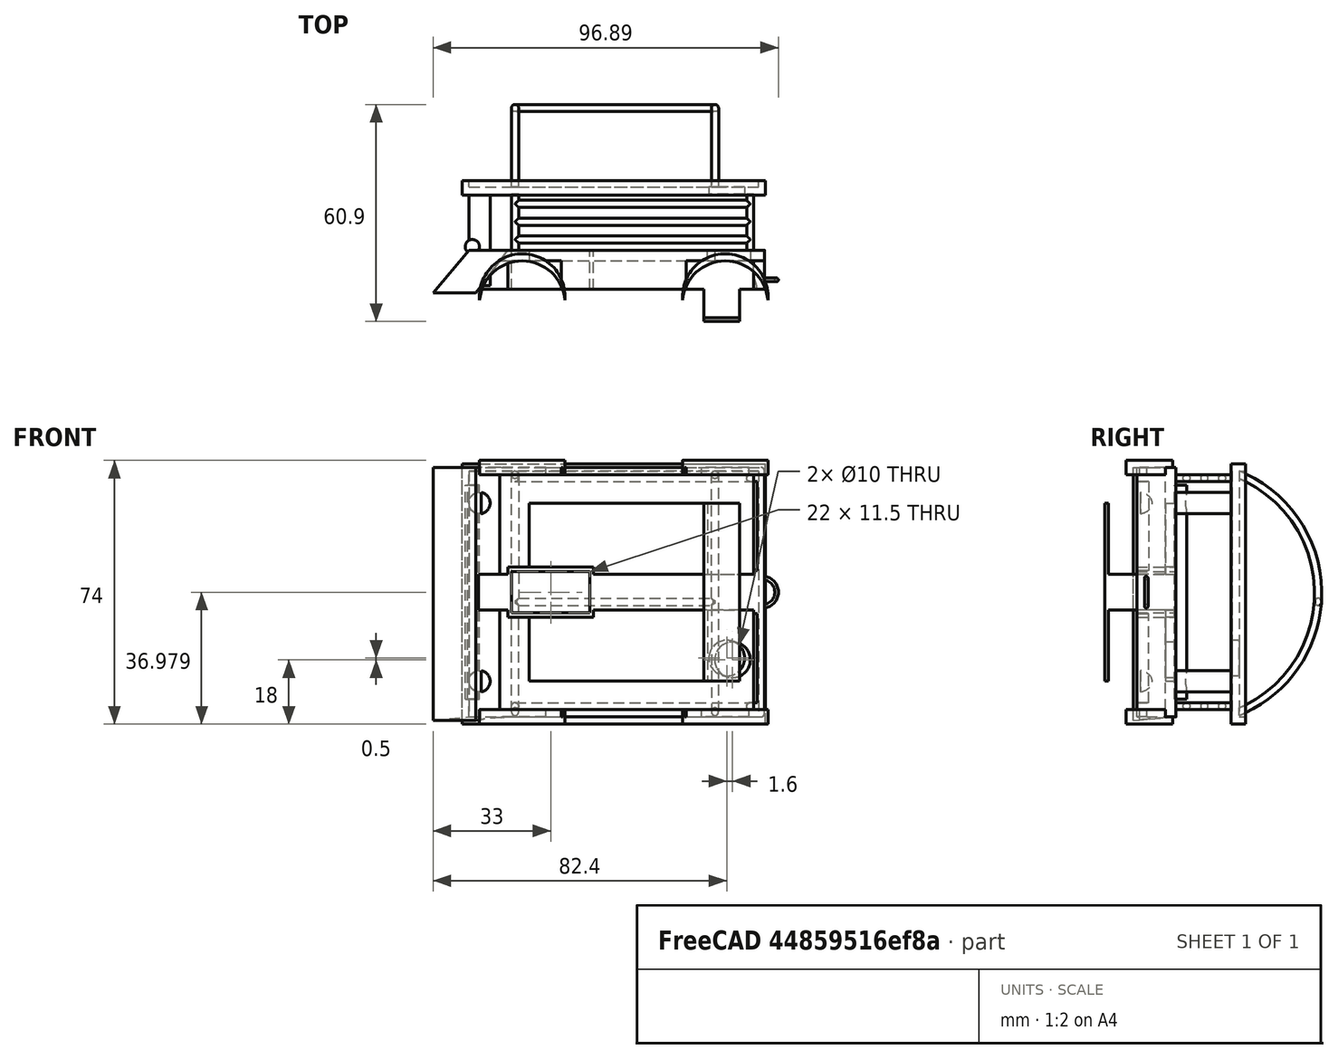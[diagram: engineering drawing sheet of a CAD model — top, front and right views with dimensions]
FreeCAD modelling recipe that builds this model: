
FCSTD DOCUMENT  (FreeCAD 0.18R4 (GitTag))
Label: Chasis Reto (Terminado)
License: All rights reserved
LicenseURL: http://en.wikipedia.org/wiki/All_rights_reserved
objects: Part::Cylinder×31, Part::Box×21, Part::MultiFuse×18, Part::Cut×15, Part::Torus×3, Part::Fillet×1, Part::Wedge×1
note: 90 computed .brp shape members not serialized (recipe doc carries the construction recipe); baked Part::Feature solids carry a one-line shape summary decoded from their .brp

FEATURE [Part::Cylinder] Cylinder  label="Cilindro"
  Angle = 360
  AttacherType = Attacher::AttachEngine3D
  Height = 4
  Radius = 12
FEATURE [Part::Cylinder] Cylinder001  label="Cilindro001"
  Angle = 360
  AttacherType = Attacher::AttachEngine3D
  Height = 4
  Placement = pos=(0,-2,0) rot=(0,0,1;0rad)
  Radius = 12
FEATURE [Part::Cut] Cut
  Base = -> Cylinder
  Placement = pos=(2,0,0) rot=(0,0,1;0rad)
  Refine = true
  Tool = -> Cylinder001
FEATURE [Part::Box] Box  label="Cubo"
  AttacherType = Attacher::AttachEngine3D
  Height = 70
  Length = 80
  Placement = pos=(-10,10,2) rot=(0,0,1;0rad)
  Width = 3
FEATURE [Part::Cylinder] Cylinder002  label="Cilindro002"
  Angle = 360
  AttacherType = Attacher::AttachEngine3D
  Height = 4
  Radius = 12
FEATURE [Part::Cylinder] Cylinder003  label="Cilindro003"
  Angle = 360
  AttacherType = Attacher::AttachEngine3D
  Height = 4
  Placement = pos=(0,-2,0) rot=(0,0,1;0rad)
  Radius = 12
FEATURE [Part::Cut] Cut001
  Base = -> Cylinder002
  Placement = pos=(2,0,70) rot=(0,0,1;0rad)
  Refine = true
  Tool = -> Cylinder003
FEATURE [Part::Cylinder] Cylinder004  label="Cilindro004"
  Angle = 360
  AttacherType = Attacher::AttachEngine3D
  Height = 4
  Radius = 12
FEATURE [Part::Cylinder] Cylinder005  label="Cilindro005"
  Angle = 360
  AttacherType = Attacher::AttachEngine3D
  Height = 4
  Placement = pos=(0,-2,0) rot=(0,0,1;0rad)
  Radius = 12
FEATURE [Part::Cut] Cut002
  Base = -> Cylinder004
  Placement = pos=(59,0,0) rot=(0,0,1;0rad)
  Refine = true
  Tool = -> Cylinder005
FEATURE [Part::Cylinder] Cylinder006  label="Cilindro006"
  Angle = 360
  AttacherType = Attacher::AttachEngine3D
  Height = 4
  Radius = 12
FEATURE [Part::Cylinder] Cylinder007  label="Cilindro007"
  Angle = 360
  AttacherType = Attacher::AttachEngine3D
  Height = 4
  Placement = pos=(0,-2,0) rot=(0,0,1;0rad)
  Radius = 12
FEATURE [Part::Cut] Cut003
  Base = -> Cylinder006
  Placement = pos=(59,0,70) rot=(0,0,1;0rad)
  Refine = true
  Tool = -> Cylinder007
FEATURE [Part::Fillet] Fillet
  Base = -> Box
  Edges = 4 edges r=1: [Edge2,Edge4,Edge6,Edge8]
FEATURE [Part::Cylinder] Cylinder009  label="Cilindro009"
  Angle = 360
  AttacherType = Attacher::AttachEngine3D
  Height = 15
  Placement = pos=(-10,18,62) rot=(1,0,0;1.5708rad)
  Radius = 3
FEATURE [Part::Cylinder] Cylinder010  label="Cilindro010"
  Angle = 360
  AttacherType = Attacher::AttachEngine3D
  Height = 60
  Placement = pos=(-12,14,7) rot=(0,0,1;0rad)
  Radius = 2
FEATURE [Part::Cylinder] Cylinder011  label="Cilindro011"
  Angle = 360
  AttacherType = Attacher::AttachEngine3D
  Height = 60
  Placement = pos=(-12,7,7) rot=(0,0,1;0rad)
  Radius = 2
FEATURE [Part::Cylinder] Cylinder012  label="Cilindro012"
  Angle = 360
  AttacherType = Attacher::AttachEngine3D
  Height = 10
  Placement = pos=(61,19,18) rot=(0.57735,0.57735,-0.57735;2.0944rad)
  Radius = 5
FEATURE [Part::Cut] Cut004
  Base = -> Fillet
  Refine = true
  Tool = -> Cylinder012
FEATURE [Part::MultiFuse] Fusion
  Refine = true
  Shapes = -> [Cut,Cut001,Cut002,Cut003]
FEATURE [Part::Cylinder] Cylinder013  label="Cilindro013"
  Angle = 360
  AttacherType = Attacher::AttachEngine3D
  Height = 15
  Placement = pos=(-10,18,12) rot=(1,0,0;1.5708rad)
  Radius = 3
FEATURE [Part::Box] Box001  label="Cubo001"
  AttacherType = Attacher::AttachEngine3D
  Height = 20
  Length = 50
  Placement = pos=(4,6,12) rot=(0,0,1;0rad)
  Width = 10
FEATURE [Part::Box] Box002  label="Cubo002"
  AttacherType = Attacher::AttachEngine3D
  Height = 20
  Length = 50
  Placement = pos=(4,6,42) rot=(0,0,1;0rad)
  Width = 10
FEATURE [Part::MultiFuse] Fusion002
  Refine = true
  Shapes = -> [Box002,Box001]
FEATURE [Part::Box] Box003  label="Cubo003"
  AttacherType = Attacher::AttachEngine3D
  Height = 2
  Length = 35
  Placement = pos=(13,2,2) rot=(0,0,1;0rad)
  Width = 10
FEATURE [Part::Box] Box004  label="Cubo004"
  AttacherType = Attacher::AttachEngine3D
  Height = 2
  Length = 35
  Placement = pos=(13,2,70) rot=(0,0,1;0rad)
  Width = 10
FEATURE [Part::Box] Box005  label="Cubo005"
  AttacherType = Attacher::AttachEngine3D
  Height = 3
  Length = 66
  Placement = pos=(67,2,70) rot=(0,1,0;1.5708rad)
  Width = 10
FEATURE [Part::Cylinder] Cylinder014  label="Cilindro014"
  Angle = 360
  AttacherType = Attacher::AttachEngine3D
  Height = 17
  Placement = pos=(0,12,5) rot=(-1,0,0;1.5708rad)
  Radius = 1
FEATURE [Part::Cylinder] Cylinder015  label="Cilindro015"
  Angle = 360
  AttacherType = Attacher::AttachEngine3D
  Height = 17
  Placement = pos=(66,12,5) rot=(-1,0,0;1.5708rad)
  Radius = 1
FEATURE [Part::Cylinder] Cylinder016  label="Cilindro016"
  Angle = 360
  AttacherType = Attacher::AttachEngine3D
  Height = 17
  Placement = pos=(66,12,69) rot=(-1,0,0;1.5708rad)
  Radius = 1
FEATURE [Part::Cylinder] Cylinder017  label="Cilindro017"
  Angle = 360
  AttacherType = Attacher::AttachEngine3D
  Height = 17
  Placement = pos=(0,12,69) rot=(-1,0,0;1.5708rad)
  Radius = 1
FEATURE [Part::Cylinder] Cylinder018  label="Cilindro018"
  Angle = 360
  AttacherType = Attacher::AttachEngine3D
  Height = 66
  Placement = pos=(7e-15,26,5) rot=(0.57735,-0.57735,0.57735;4.18879rad)
  Radius = 1
FEATURE [Part::Cylinder] Cylinder019  label="Cilindro019"
  Angle = 360
  AttacherType = Attacher::AttachEngine3D
  Height = 66
  Placement = pos=(7e-15,21,5) rot=(0.57735,-0.57735,0.57735;4.18879rad)
  Radius = 1
FEATURE [Part::Cylinder] Cylinder020  label="Cilindro020"
  Angle = 360
  AttacherType = Attacher::AttachEngine3D
  Height = 66
  Placement = pos=(7e-15,16,5) rot=(0.57735,-0.57735,0.57735;4.18879rad)
  Radius = 1
FEATURE [Part::Cylinder] Cylinder021  label="Cilindro021"
  Angle = 360
  AttacherType = Attacher::AttachEngine3D
  Height = 66
  Placement = pos=(7e-15,16,69) rot=(0.57735,-0.57735,0.57735;4.18879rad)
  Radius = 1
FEATURE [Part::Cylinder] Cylinder022  label="Cilindro022"
  Angle = 360
  AttacherType = Attacher::AttachEngine3D
  Height = 66
  Placement = pos=(7e-15,21,69) rot=(0.57735,-0.57735,0.57735;4.18879rad)
  Radius = 1
FEATURE [Part::Cylinder] Cylinder023  label="Cilindro023"
  Angle = 360
  AttacherType = Attacher::AttachEngine3D
  Height = 66
  Placement = pos=(7e-15,26,69) rot=(0.57735,-0.57735,0.57735;4.18879rad)
  Radius = 1
FEATURE [Part::Torus] Torus  label="Toro"
  Angle1 = -180
  Angle2 = 180
  Angle3 = 360
  AttacherType = Attacher::AttachEngine3D
  Placement = pos=(69.3867,4.65874,37) rot=(0.57735,0.57735,-0.57735;2.0944rad)
  Radius1 = 4
  Radius2 = 0.5
FEATURE [Part::Box] Box006  label="Cubo006"
  AttacherType = Attacher::AttachEngine3D
  Height = 10
  Length = 80
  Placement = pos=(-11,2,32) rot=(0,0,1;0rad)
  Width = 10
FEATURE [Part::MultiFuse] Fusion001
  Refine = true
  Shapes = -> [Cylinder013,Fusion,Cylinder011,Cylinder010,Cylinder009,Cut004]
FEATURE [Part::Cut] Cut005
  Base = -> Fusion001
  Refine = true
  Tool = -> Fusion002
FEATURE [Part::MultiFuse] Fusion003
  Refine = true
  Shapes = -> [Cut005,Box003,Box004,Box005,Cylinder014,Cylinder015,Cylinder016,Cylinder017,Cylinder020,Cylinder018,Cylinder019,Cylinder021,Cylinder022,Cylinder023,Box006,Torus]
FEATURE [Part::Wedge] Wedge  label="Cuña"
  AttacherType = Attacher::AttachEngine3D
  Placement = pos=(-15,5,11) rot=(0,0,1;0rad)
  X2max = 13
  X2min = 2
  Xmax = 4
  Xmin = -8
  Ymax = 8
  Ymin = -4
  Z2max = 61
  Z2min = -9
  Zmax = 61
  Zmin = -10
FEATURE [Part::MultiFuse] Fusion004
  Refine = true
  Shapes = -> [Wedge,Fusion003]
FEATURE [Part::Cylinder] Cylinder024  label="Cilindro024"
  Angle = 360
  AttacherType = Attacher::AttachEngine3D
  Height = 25
  Placement = pos=(0,0,8) rot=(0,0,1;0rad)
  Radius = 10
FEATURE [Part::Cylinder] Cylinder025  label="Cilindro025"
  Angle = 360
  AttacherType = Attacher::AttachEngine3D
  Height = 8
  Radius = 0.5
FEATURE [Part::MultiFuse] Fusion005
  Placement = pos=(0,0,-51) rot=(0,0,1;0rad)
  Refine = true
  Shapes = -> [Cylinder025,Cylinder024]
FEATURE [Part::Box] Box007  label="Cubo007"
  AttacherType = Attacher::AttachEngine3D
  Height = 32
  Length = 16
  Placement = pos=(-8,-17,-49) rot=(0,0,1;0rad)
  Width = 10
FEATURE [Part::Box] Box008  label="Cubo008"
  AttacherType = Attacher::AttachEngine3D
  Height = 32
  Length = 16
  Placement = pos=(-8,7,-49) rot=(0,0,1;0rad)
  Width = 10
FEATURE [Part::Cut] Cut006
  Base = -> Fusion005
  Refine = true
  Tool = -> Box007
FEATURE [Part::Cut] Cut007
  Base = -> Cut006
  Placement = pos=(58,1,49) rot=(0,0,1;0rad)
  Refine = true
  Tool = -> Box008
FEATURE [Part::Cut] Cut010
  Base = -> Fusion004
  Refine = true
  Tool = -> Cut007
FEATURE [Part::Box] Box011  label="Cubo011"
  AttacherType = Attacher::AttachEngine3D
  Height = 10
  Length = 10
  Placement = pos=(53,-7,32) rot=(0,0,1;0rad)
  Width = 10
FEATURE [Part::MultiFuse] Fusion007
  Refine = true
  Shapes = -> [Cut010,Box011]
FEATURE [Part::Box] Box012  label="Cubo012"
  AttacherType = Attacher::AttachEngine3D
  Height = 50
  Length = 10
  Placement = pos=(53,-7,12) rot=(0,0,1;0rad)
  Width = 1
FEATURE [Part::MultiFuse] Fusion008
  Refine = true
  Shapes = -> [Box012,Fusion007]
FEATURE [Part::Cylinder] Cylinder028  label="Cilindro028"
  Angle = 360
  AttacherType = Attacher::AttachEngine3D
  Height = 25
  Placement = pos=(0,0,8) rot=(0,0,1;0rad)
  Radius = 10
FEATURE [Part::Box] Box013  label="Cubo013"
  AttacherType = Attacher::AttachEngine3D
  Height = 32
  Length = 16
  Placement = pos=(-8,7,-49) rot=(0,0,1;0rad)
  Width = 10
FEATURE [Part::Cylinder] Cylinder029  label="Cilindro029"
  Angle = 360
  AttacherType = Attacher::AttachEngine3D
  Height = 8
  Radius = 0.5
FEATURE [Part::Box] Box014  label="Cubo014"
  AttacherType = Attacher::AttachEngine3D
  Height = 32
  Length = 16
  Placement = pos=(-8,-17,-49) rot=(0,0,1;0rad)
  Width = 10
FEATURE [Part::MultiFuse] Fusion009
  Placement = pos=(0,0,-51) rot=(0,0,1;0rad)
  Refine = true
  Shapes = -> [Cylinder029,Cylinder028]
FEATURE [Part::Cut] Cut012
  Base = -> Fusion009
  Refine = true
  Tool = -> Box014
FEATURE [Part::Cut] Cut011
  Base = -> Cut012
  Placement = pos=(58,1,25) rot=(1,0,0;3.14159rad)
  Refine = true
  Tool = -> Box013
FEATURE [Part::Cut] Cut013
  Base = -> Fusion008
  Refine = true
  Tool = -> Cut011
FEATURE [Part::Box] Box016  label="Cubo016"
  AttacherType = Attacher::AttachEngine3D
  Height = 14
  Length = 24
  Placement = pos=(-2,2,30) rot=(0,0,1;0rad)
  Width = 11
FEATURE [Part::MultiFuse] Fusion010
  Refine = true
  Shapes = -> [Cut013,Box016]
FEATURE [Part::Box] Box015  label="Cubo015"
  AttacherType = Attacher::AttachEngine3D
  Height = 27
  Length = 22
  Placement = pos=(-1,-0.95555,42.7291) rot=(-1,0,0;1.5708rad)
  Width = 11.5
FEATURE [Part::Cut] Cut014
  Base = -> Fusion010
  Refine = true
  Tool = -> Box015
FEATURE [Part::Cylinder] Cylinder030  label="Cilindro030"
  Angle = 360
  AttacherType = Attacher::AttachEngine3D
  Height = 14
  Placement = pos=(-10,15.1,12) rot=(1,0,0;4.71239rad)
  Radius = 3
FEATURE [Part::Cylinder] Cylinder031  label="Cilindro031"
  Angle = 360
  AttacherType = Attacher::AttachEngine3D
  Height = 14
  Placement = pos=(-10,15.1,62) rot=(-1,0,0;1.5708rad)
  Radius = 3
FEATURE [Part::MultiFuse] Fusion011
  Refine = true
  Shapes = -> [Cylinder031,Cylinder030]
FEATURE [Part::MultiFuse] Fusion012
  Refine = true
  Shapes = -> [Fusion011,Cut014]
FEATURE [Part::Box] Box017  label="Cubo017"
  AttacherType = Attacher::AttachEngine3D
  Height = 72
  Length = 85
  Placement = pos=(-14.9,28.7,0.6) rot=(0,0,1;0rad)
  Width = 2
FEATURE [Part::MultiFuse] Fusion013
  Refine = true
  Shapes = -> [Box017,Fusion012]
FEATURE [Part::Box] Box018  label="Cubo018"
  AttacherType = Attacher::AttachEngine3D
  Height = 73
  Length = 2
  Placement = pos=(-14.9,28.5,0) rot=(0,0,1;0rad)
  Width = 4
FEATURE [Part::Box] Box019  label="Cubo019"
  AttacherType = Attacher::AttachEngine3D
  Height = 73
  Length = 2
  Placement = pos=(68.3,28.5,0) rot=(0,0,1;0rad)
  Width = 4
FEATURE [Part::Box] Box020  label="Cubo020"
  AttacherType = Attacher::AttachEngine3D
  Height = 82
  Length = 2
  Placement = pos=(68.4,28.5,3e-16) rot=(0,1,0;4.71239rad)
  Width = 4
FEATURE [Part::Box] Box021  label="Cubo021"
  AttacherType = Attacher::AttachEngine3D
  Height = 82
  Length = 2
  Placement = pos=(68.8,28.5,71) rot=(0,-1,0;1.5708rad)
  Width = 4
FEATURE [Part::MultiFuse] Fusion014
  Refine = true
  Shapes = -> [Box021,Box020,Box019,Box018]
FEATURE [Part::MultiFuse] Fusion015
  Placement = pos=(0,4.2,-0.7) rot=(0,0,1;0rad)
  Refine = true
  Shapes = -> [Fusion013,Fusion014]
FEATURE [Part::Torus] Torus001  label="Toro001"
  Angle1 = -180
  Angle2 = 180
  Angle3 = 360
  AttacherType = Attacher::AttachEngine3D
  Placement = pos=(-3.98e-14,21.1,136.6) rot=(0,1,0;4.71239rad)
  Radius1 = 36
  Radius2 = 1
FEATURE [Part::Torus] Torus002  label="Toro002"
  Angle1 = -180
  Angle2 = 180
  Angle3 = 360
  AttacherType = Attacher::AttachEngine3D
  Placement = pos=(56.1,21.1,136.6) rot=(0,-1,0;1.5708rad)
  Radius1 = 36
  Radius2 = 1
FEATURE [Part::MultiFuse] Fusion016
  Refine = true
  Shapes = -> [Torus002,Torus001]
FEATURE [Part::Box] Box022  label="Cubo022"
  AttacherType = Attacher::AttachEngine3D
  Height = 85
  Length = 110
  Placement = pos=(-22.6,-21.3,94.1) rot=(0,0,1;0rad)
  Width = 56
FEATURE [Part::Cut] Cut015
  Base = -> Fusion016
  Placement = pos=(0,0,-100.6) rot=(0,0,1;0rad)
  Refine = true
  Tool = -> Box022
FEATURE [Part::MultiFuse] Fusion017
  Refine = true
  Shapes = -> [Fusion015,Cut015]
FEATURE [Part::Cylinder] Cylinder032  label="Cilindro032"
  Angle = 360
  AttacherType = Attacher::AttachEngine3D
  Height = 56
  Placement = pos=(0.1,57.1,33.6) rot=(0,1,0;1.5708rad)
  Radius = 1
FEATURE [Part::MultiFuse] Fusion018
  Refine = true
  Shapes = -> [Cylinder032,Fusion017]
FEATURE [Part::Cylinder] Cylinder033  label="Cilindro033"
  Angle = 360
  AttacherType = Attacher::AttachEngine3D
  Height = 10
  Placement = pos=(59.4,39.3,17.8) rot=(1,0,0;1.5708rad)
  Radius = 5
FEATURE [Part::Cut] Cut016
  Base = -> Fusion018
  Refine = true
  Tool = -> Cylinder033
